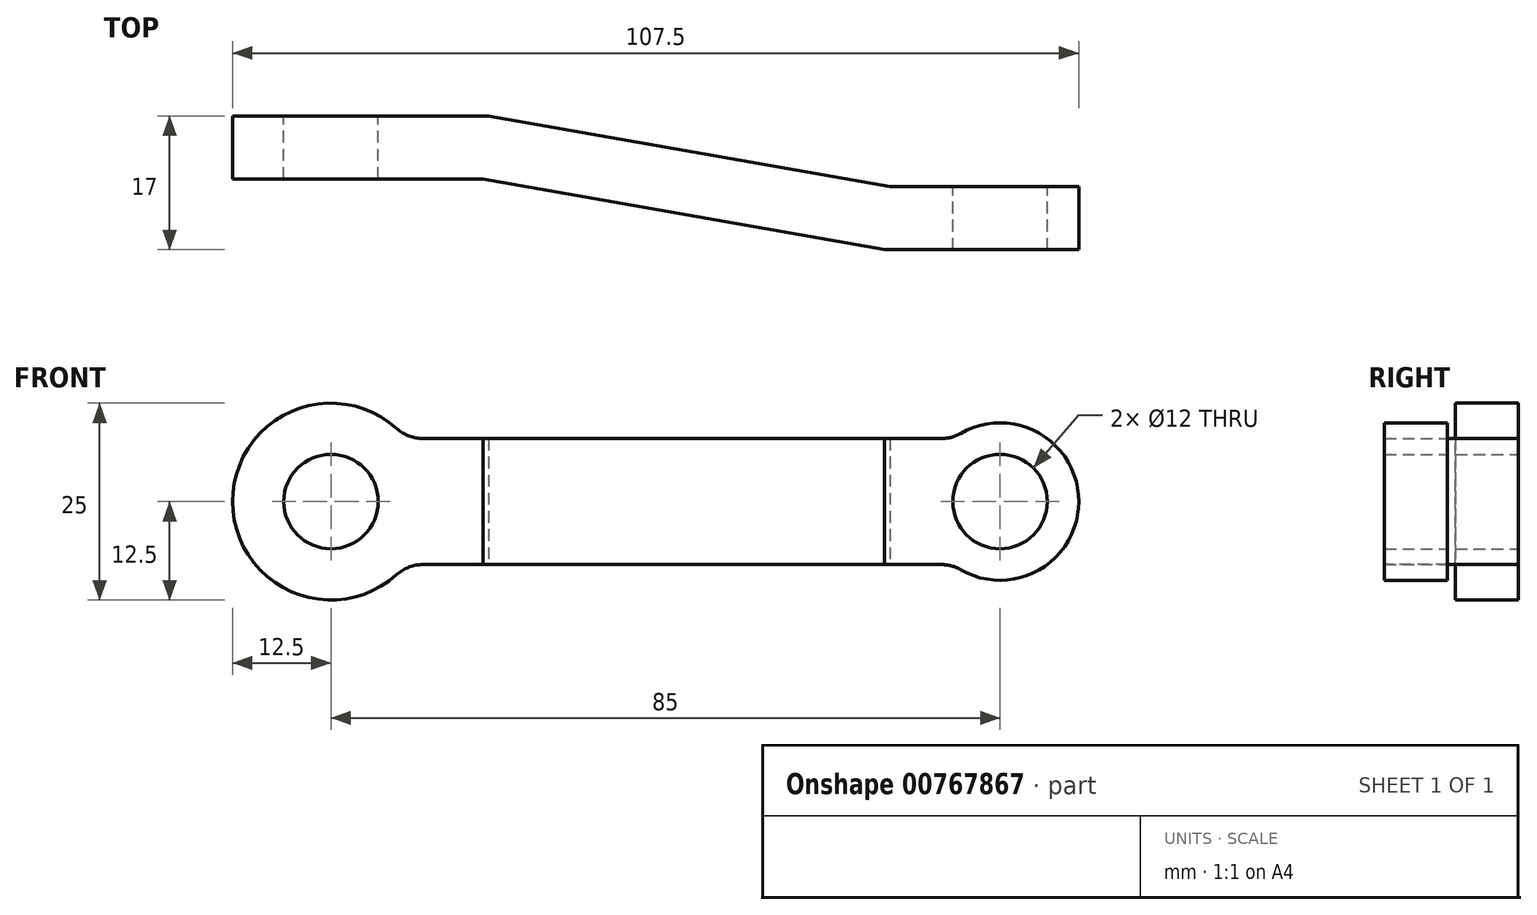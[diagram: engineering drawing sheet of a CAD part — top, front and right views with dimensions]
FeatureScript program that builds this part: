
annotation { "Feature Type Name" : "Feature", "Feature Type Description" : "" }
export const myFeature = defineFeature(function(context is Context, id is Id, definition is map)
    precondition{}
    {
        {
            var Q0;
            Q0=qCreatedBy(makeId("Front.planeOp"),FACE);
            var sketch = newSketch(context, id + "F0", { "sketchPlane" : qUnion([Q0])});
            skCircle(sketch, "E0", {"center": v(0, 0) * mm, "radius": 12.5 * mm});
            skCircle(sketch, "E1", {"center": v(85, 0) * mm, "radius": 10 * mm});
            skLineSegment(sketch, "E2", {"start": v(85, 0) * mm, "end": v(0, 0) * mm, "construction": true});
            skLineSegment(sketch, "E3", {"start": v(9.6, 8) * mm, "end": v(79, 8) * mm});
            skLineSegment(sketch, "E4.MirrorCS", {"start": v(9.6, -8) * mm, "end": v(79, -8) * mm});
            skCircle(sketch, "E5", {"center": v(0, 0) * mm, "radius": 6 * mm});
            skCircle(sketch, "E6", {"center": v(85, 0) * mm, "radius": 6 * mm});
            skSolve(sketch);
        }
        {
            var Q0;
            Q0 = qSketchRegion(id + "F0", true);
            extrude(context, id + "F1", {"entities" : qUnion([Q0]), "depth" : 25 * mm, "offsetDistance" : 25 * mm});
        }
        {
            var Q0;
            Q0=qCreatedBy(makeId("Top.planeOp"),FACE);
            var sketch = newSketch(context, id + "F2", { "sketchPlane" : qUnion([Q0])});
            skLineSegment(sketch, "E7", {"start": v(-12.5, 0) * mm, "end": v(20, 0) * mm});
            skLineSegment(sketch, "E8", {"start": v(20, 0) * mm, "end": v(71.04, -9) * mm});
            skLineSegment(sketch, "E9", {"start": v(71.04, -9) * mm, "end": v(95, -9) * mm});
            skLineSegment(sketch, "E10.0", {"start": v(70.34, -17) * mm, "end": v(95, -17) * mm});
            skLineSegment(sketch, "E10.1", {"start": v(19.3, -8) * mm, "end": v(70.34, -17) * mm});
            skLineSegment(sketch, "E10.2", {"start": v(-12.5, -8) * mm, "end": v(19.3, -8) * mm});
            skLineSegment(sketch, "E11", {"start": v(-12.5, 0) * mm, "end": v(-12.5, -8) * mm});
            skLineSegment(sketch, "E12", {"start": v(95, -9) * mm, "end": v(95, -17) * mm});
            skLineSegment(sketch, "E13", {"start": v(95, 0) * mm, "end": v(95, -25) * mm});
            skLineSegment(sketch, "E14", {"start": v(-12.5, -25) * mm, "end": v(-12.5, 0) * mm});
            skSolve(sketch);
        }
        {
            var Q0;
            Q0=makeQuery(id+"F2.imprint","IMPRINT",FACE,{"disambiguationData":[TD([[makeQuery(id+"F2.imprint","IMPRINT",EDGE,{"derivedFrom":sQuery(id+"F2.wireOp",EDGE,"E7")}),-1.0]])]});
            extrude(context, id + "F3", {"entities" : qUnion([Q0]), "operationType" : NewBodyOperationType.INTERSECT, "endBound" : BoundingType.SYMMETRIC, "depth" : 25 * mm, "offsetDistance" : 25 * mm});
        }
        {
            var Q0;
            Q0=makeQuery(id+"F1.opExtrude","SWEPT_EDGE",EDGE,{"disambiguationData":[OSD([sQuery(id+"F0.wireOp",EDGE,"E1"),sQuery(id+"F0.wireOp",EDGE,"E3")])]});
            var Q1;
            Q1=makeQuery(id+"F1.opExtrude","SWEPT_EDGE",EDGE,{"disambiguationData":[OSD([sQuery(id+"F0.wireOp",EDGE,"E0"),sQuery(id+"F0.wireOp",EDGE,"E3")])]});
            var Q2;
            Q2=makeQuery(id+"F1.opExtrude","SWEPT_EDGE",EDGE,{"disambiguationData":[OSD([sQuery(id+"F0.wireOp",EDGE,"E1"),sQuery(id+"F0.wireOp",EDGE,"E4.MirrorCS")])]});
            var Q3;
            Q3=makeQuery(id+"F1.opExtrude","SWEPT_EDGE",EDGE,{"disambiguationData":[OSD([sQuery(id+"F0.wireOp",EDGE,"E0"),sQuery(id+"F0.wireOp",EDGE,"E4.MirrorCS")])]});
            fillet(context, id + "F4", {"entities" : qUnion([Q0, Q1, Q2, Q3]), "radius" : 5 * mm, "tangentPropagation" : true, "allowEdgeOverflow" : false});
        }
    });
